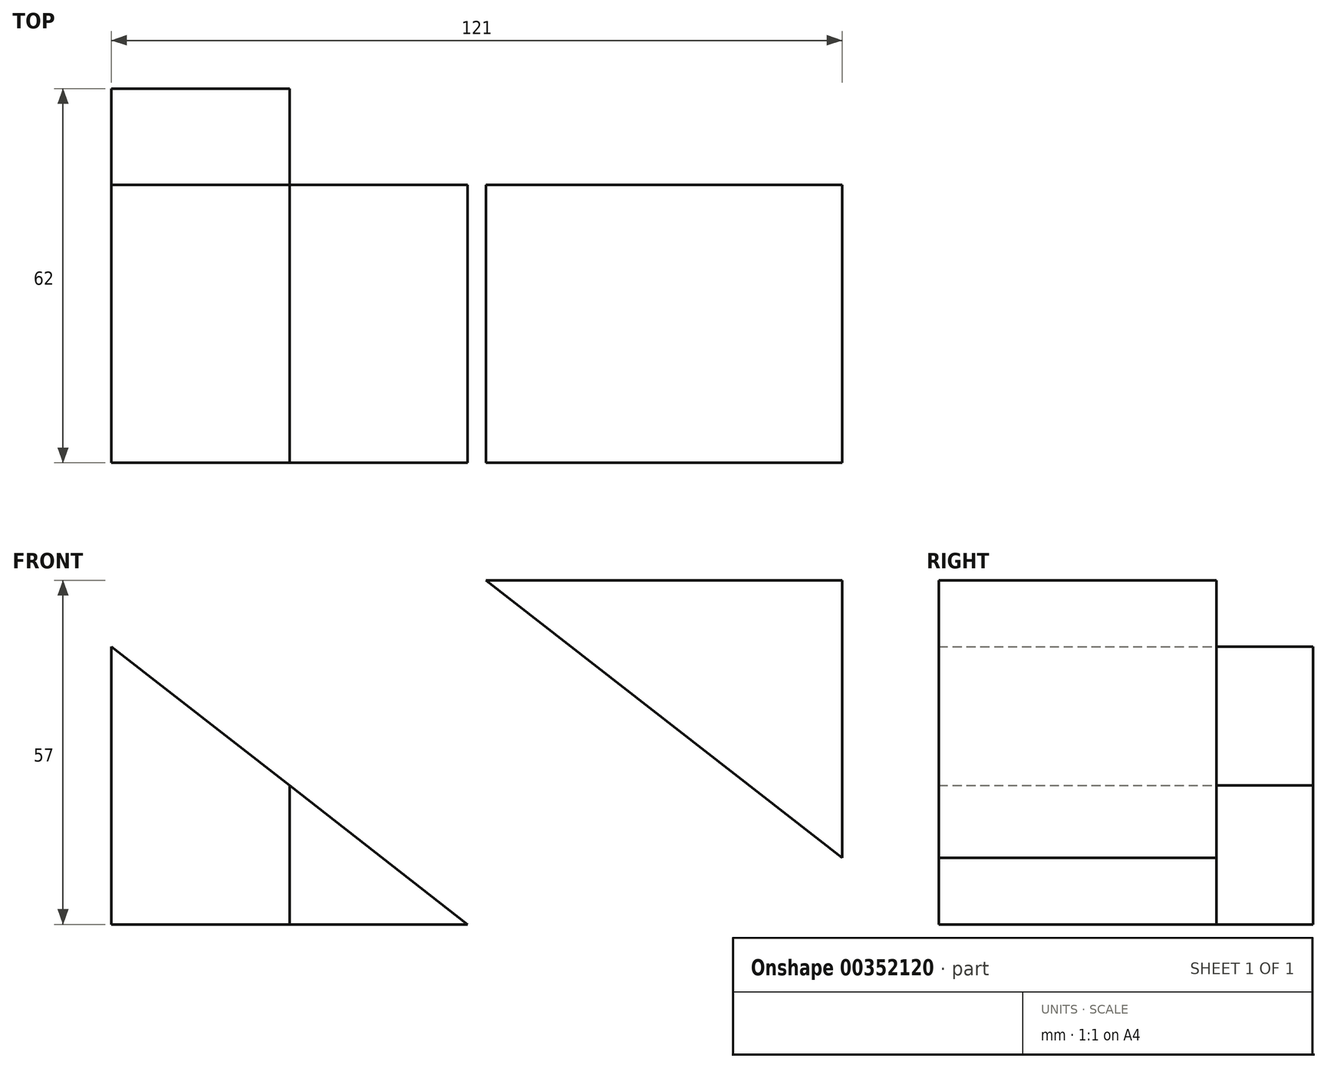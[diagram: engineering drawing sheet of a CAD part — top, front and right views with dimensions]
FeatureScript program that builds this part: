
annotation { "Feature Type Name" : "Feature", "Feature Type Description" : "" }
export const myFeature = defineFeature(function(context is Context, id is Id, definition is map)
    precondition{}
    {
        {
            var Q0;
            Q0=qCreatedBy(makeId("Front.planeOp"),FACE);
            var sketch = newSketch(context, id + "F0", { "sketchPlane" : qUnion([Q0])});
            skLineSegment(sketch, "E0.bottom", {"start": v(0, 0) * mm, "end": v(121, 0) * mm});
            skLineSegment(sketch, "E0.top", {"start": v(0, 57) * mm, "end": v(121, 57) * mm});
            skLineSegment(sketch, "E0.left", {"start": v(0, 0) * mm, "end": v(0, 57) * mm});
            skLineSegment(sketch, "E0.right", {"start": v(121, 0) * mm, "end": v(121, 57) * mm});
            skLineSegment(sketch, "E1", {"start": v(0, 46) * mm, "end": v(59, 0) * mm});
            skLineSegment(sketch, "E2", {"start": v(29.5, 23) * mm, "end": v(29.5, 0) * mm});
            skLineSegment(sketch, "E3", {"start": v(0, 46) * mm, "end": v(0, 0) * mm});
            skLineSegment(sketch, "E4", {"start": v(59, 0) * mm, "end": v(0, 46) * mm});
            skLineSegment(sketch, "E5", {"start": v(62, 57) * mm, "end": v(121, 11) * mm});
            skLineSegment(sketch, "E6", {"start": v(121, 11) * mm, "end": v(121, 57) * mm});
            skCircle(sketch, "E7", {"center": v(44, 41) * mm, "radius": 7 * mm});
            skCircle(sketch, "E8", {"center": v(77, 12) * mm, "radius": 7 * mm});
            skSolve(sketch);
        }
        {
            var Q0;
            {var subQ2=sQuery(id+"F0.wireOp",EDGE,"E5");Q0=makeQuery(id+"F0.imprint","IMPRINT",FACE,{"disambiguationData":[TD([[makeQuery(id+"F0.imprint","IMPRINT",EDGE,{"derivedFrom":subQ2}),1.0]])]});}
            extrude(context, id + "F1", {"entities" : qUnion([Q0]), "depth" : 46 * mm});
        }
        {
            var Q0;
            {var subQ2=sQuery(id+"F0.wireOp",EDGE,"E2");Q0=makeQuery(id+"F0.imprint","IMPRINT",FACE,{"disambiguationData":[TD([[makeQuery(id+"F0.imprint","IMPRINT",EDGE,{"derivedFrom":subQ2}),-1.0]])]});}
            extrude(context, id + "F2", {"entities" : qUnion([Q0]), "depth" : 46 * mm});
        }
        {
            var Q0;
            {var subQ1=sQuery(id+"F0.wireOp",EDGE,"E0.left");Q0=makeQuery(id+"F0.imprint","IMPRINT",FACE,{"disambiguationData":[TD([[makeQuery(id+"F0.imprint","IMPRINT",EDGE,{"derivedFrom":subQ1}),-1.0]])]});}
            extrude(context, id + "F3", {"entities" : qUnion([Q0]), "oppositeDirection" : true, "depth" : 16 * mm});
        }
        {
            var Q0;
            {var subQ0=sQuery(id+"F0.wireOp",EDGE,"E2");Q0=makeQuery(id+"F0.imprint","IMPRINT",FACE,{"disambiguationData":[TD([[makeQuery(id+"F0.imprint","IMPRINT",EDGE,{"derivedFrom":subQ0}),1.0]])]});}
            extrude(context, id + "F4", {"entities" : qUnion([Q0]), "depth" : 46 * mm});
        }
    });
